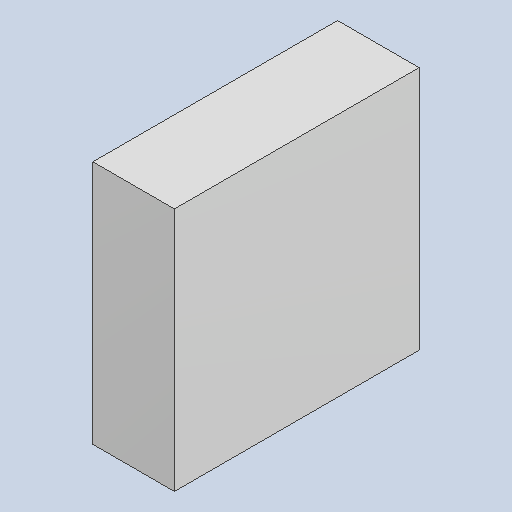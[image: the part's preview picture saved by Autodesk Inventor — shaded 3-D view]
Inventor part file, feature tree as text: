
AUTODESK INVENTOR PART (.ipt)
format: ipt  version: 2023.4 (Build 274418000, 418)  size: 81,408 bytes
history: native  units: mm
features: extrude x1
ambient origin geometry x8: Origin, YZ Plane, XZ Plane, XY Plane, X Axis, Y Axis, Z Axis, Center Point
bodies: Solid1 (feature_tree)
feature tree (1):
  extrude  "Extruded_18"  [1 undecoded]
note: 1 required parameter value undecoded (feature->parameter linkage not recoverable at this tier; creation-order binding heuristic only, values carry confidence <= 0.55)
